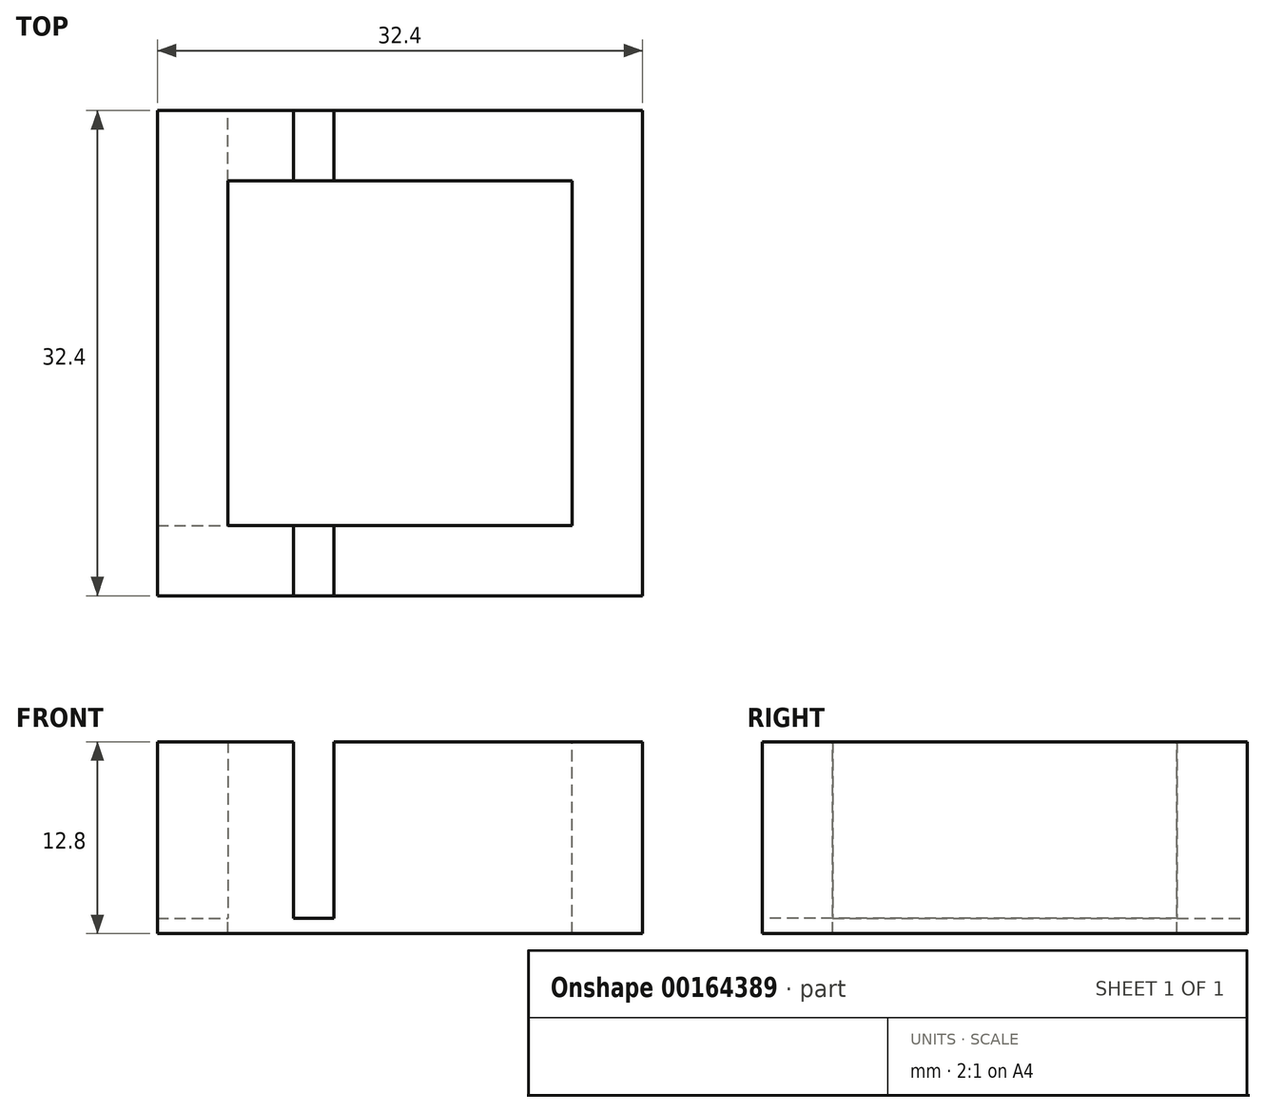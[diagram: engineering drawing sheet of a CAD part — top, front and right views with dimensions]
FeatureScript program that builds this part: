
annotation { "Feature Type Name" : "Feature", "Feature Type Description" : "" }
export const myFeature = defineFeature(function(context is Context, id is Id, definition is map)
    precondition{}
    {
        {
            var Q0;
            Q0=qCreatedBy(makeId("Top.planeOp"),FACE);
            var sketch = newSketch(context, id + "F0", { "sketchPlane" : qUnion([Q0])});
            skLineSegment(sketch, "E0.bottom", {"start": v(-8.06, 12.17) * mm, "end": v(14.94, 12.17) * mm});
            skLineSegment(sketch, "E0.top", {"start": v(-8.06, -10.83) * mm, "end": v(14.94, -10.83) * mm});
            skLineSegment(sketch, "E0.left", {"start": v(-8.06, 12.17) * mm, "end": v(-8.06, -10.83) * mm});
            skLineSegment(sketch, "E0.right", {"start": v(14.94, 12.17) * mm, "end": v(14.94, -10.83) * mm});
            skLineSegment(sketch, "E1.bottom", {"start": v(-8.06, 12.17) * mm, "end": v(19.64, 12.17) * mm});
            skLineSegment(sketch, "E1.top", {"start": v(-8.06, 16.87) * mm, "end": v(19.64, 16.87) * mm});
            skLineSegment(sketch, "E1.left", {"start": v(-8.06, 12.17) * mm, "end": v(-8.06, 16.87) * mm});
            skLineSegment(sketch, "E1.right", {"start": v(19.64, 12.17) * mm, "end": v(19.64, 16.87) * mm});
            skLineSegment(sketch, "E2.bottom", {"start": v(19.64, 12.17) * mm, "end": v(14.94, 12.17) * mm});
            skLineSegment(sketch, "E2.top", {"start": v(19.64, -15.53) * mm, "end": v(14.94, -15.53) * mm});
            skLineSegment(sketch, "E2.left", {"start": v(19.64, 12.17) * mm, "end": v(19.64, -15.53) * mm});
            skLineSegment(sketch, "E2.right", {"start": v(14.94, 12.17) * mm, "end": v(14.94, -15.53) * mm});
            skLineSegment(sketch, "E3.bottom", {"start": v(14.94, -15.53) * mm, "end": v(-12.76, -15.53) * mm});
            skLineSegment(sketch, "E3.top", {"start": v(14.94, -10.83) * mm, "end": v(-12.76, -10.83) * mm});
            skLineSegment(sketch, "E3.left", {"start": v(14.94, -15.53) * mm, "end": v(14.94, -10.83) * mm});
            skLineSegment(sketch, "E3.right", {"start": v(-12.76, -15.53) * mm, "end": v(-12.76, -10.83) * mm});
            skLineSegment(sketch, "E4.bottom", {"start": v(-12.76, -10.83) * mm, "end": v(-8.06, -10.83) * mm});
            skLineSegment(sketch, "E4.top", {"start": v(-12.76, 16.87) * mm, "end": v(-8.06, 16.87) * mm});
            skLineSegment(sketch, "E4.left", {"start": v(-12.76, -10.83) * mm, "end": v(-12.76, 16.87) * mm});
            skLineSegment(sketch, "E4.right", {"start": v(-8.06, -10.83) * mm, "end": v(-8.06, 16.87) * mm});
            skSolve(sketch);
        }
        {
            var Q0;
            {var subQ0=sQuery(id+"F0.wireOp",EDGE,"E1.bottom");Q0=makeQuery(id+"F0.imprint","IMPRINT",FACE,{"disambiguationData":[TD([[makeQuery(id+"F0.imprint","IMPRINT",EDGE,{"derivedFrom":subQ0}),-1.0]])]});}
            var Q1;
            Q1=makeQuery(id+"F0.imprint","IMPRINT",FACE,{"disambiguationData":[TD([[makeQuery(id+"F0.imprint","IMPRINT",EDGE,{"derivedFrom":sQuery(id+"F0.wireOp",EDGE,"E3.bottom")}),-1.0]])]});
            var Q2;
            {var subQ2=sQuery(id+"F0.wireOp",EDGE,"E4.bottom");Q2=makeQuery(id+"F0.imprint","IMPRINT",FACE,{"disambiguationData":[TD([[makeQuery(id+"F0.imprint","IMPRINT",EDGE,{"derivedFrom":subQ2}),1.0]])]});}
            var Q3;
            {var subQ1=sQuery(id+"F0.wireOp",EDGE,"E1.bottom");Q3=makeQuery(id+"F0.imprint","IMPRINT",FACE,{"disambiguationData":[TD([[makeQuery(id+"F0.imprint","IMPRINT",EDGE,{"derivedFrom":subQ1}),1.0]])]});}
            var Q4;
            Q4=makeQuery(id+"F0.imprint","IMPRINT",FACE,{"disambiguationData":[TD([[makeQuery(id+"F0.imprint","IMPRINT",EDGE,{"derivedFrom":sQuery(id+"F0.wireOp",EDGE,"E2.bottom")}),1.0]])]});
            extrude(context, id + "F1", {"entities" : qUnion([Q0, Q1, Q2, Q3, Q4]), "oppositeDirection" : true, "depth" : 1 * mm});
        }
        {
            var Q0;
            Q0 = qSketchRegion(id + "F0", true);
            extrude(context, id + "F2", {"entities" : qUnion([Q0]), "operationType" : NewBodyOperationType.ADD, "depth" : 11.8 * mm});
        }
        {
            var Q0;
            {var subQ0=sQuery(id+"F0.wireOp",EDGE,"E3.bottom");var subQ1=sQuery(id+"F0.wireOp",EDGE,"E2.top");Q0=makeQuery(id+"F2.boolean.opBoolean","MERGE",FACE,{"derivedFrom":[makeQuery(id+"F1.opExtrude","SWEPT_FACE",FACE,{"disambiguationData":[OSD([subQ1,subQ0])]}),makeQuery(id+"F2.opExtrude","SWEPT_FACE",FACE,{"disambiguationData":[OSD([subQ1,subQ0])]})]});}
            var sketch = newSketch(context, id + "F3", { "sketchPlane" : qUnion([Q0])});
            skLineSegment(sketch, "E5.bottom", {"start": v(-3.66, 11.8) * mm, "end": v(-0.96, 11.8) * mm});
            skLineSegment(sketch, "E5.top", {"start": v(-3.66, 0) * mm, "end": v(-0.96, 0) * mm});
            skLineSegment(sketch, "E5.left", {"start": v(-3.66, 11.8) * mm, "end": v(-3.66, 0) * mm});
            skLineSegment(sketch, "E5.right", {"start": v(-0.96, 11.8) * mm, "end": v(-0.96, 0) * mm});
            skSolve(sketch);
        }
        {
            var Q0;
            Q0=makeQuery(id+"F3.imprint","IMPRINT",FACE,{"disambiguationData":[TD([[makeQuery(id+"F3.imprint","IMPRINT",EDGE,{"derivedFrom":sQuery(id+"F3.wireOp",EDGE,"E5.bottom")}),1.0]])]});
            extrude(context, id + "F4", {"entities" : qUnion([Q0]), "operationType" : NewBodyOperationType.REMOVE, "endBound" : BoundingType.THROUGH_ALL, "oppositeDirection" : true, "depth" : 25 * mm});
        }
    });
